# Revit family: Groeninger Window Drives
name_source: partatom
category: Fenster
units: mm (PartAtom-declared; Revit-internal decimal feet)

## family parameters
Basisbauteil = Fläche
Beim Laden mit Abzugskörper schneiden = Nein
Gemeinsam genutzt = Nein
OmniClass-Nummer = 23.30.20.11
OmniClass-Titel = Window Components
Raumberechnungspunkt = Nein

## types (1)
- Window actuator DK-100 (Art. No. G1001000)
    Accessories = No additional components required, such as brackets for drive attachment or elements for transmitting the drive force, are required
    Building Management System / Smart Home = Integration into the building management system through potential-free normally open contact (digital IO)
    Center sealing = Center sealing systems required
    City = Aichtal
    Control = Pushbuttons, switches, dead man's buttons
    Country = Germany
    Description = Window drive for automated tilt-opening and tilt-closing including locking and unlocking, with full retention of manual operation in any window position and completely concealed frame mounting
    Detection of window position = Detection of the window position integrated in the drive during automatic and manual operation
    Duty cycle (DIN EN 60034-1) = S3 25%; S2 2min
    End positions = Automated referencing of end positions
    Fastening = Sufficient material available for screw fastening
    Groove position = 13mm
    Hersteller = Groeninger Antriebstechnik GmbH & Co. KG
    Hinge side = Hinge side right and left possible
    Installation position = Completely concealed drive milled into the profile, invisible in closed position
    Lifetime = Tested with 20,000 switching cycles (double stroke incl. locking)
    Manual operation = Manual operation of all window positions (tilt position, turning position, closed position) by window handle possible from any position (window handle permanently mounted)
    Modell = Fensterantrieb DK-100 (Art. Nr.: G1001000)
    Opening / Closing Time = approx. 28s in normal mode and approx. 35s in slow mode
    Opening and closing force = 800N via the locking bar
    Opening width = Tilt opening width between 100 mm and 130 mm depending on the fitting used
    Possible fittings = Winkhaus activPilot Ergo, Maco Multi Comfort Fitting
    Rated current consumption = 0.75 A
    Rebate space = 12-14mm
    Reduced speed = Slow mode adjustable via DIP switch to realize quiet running noise
    Risidual ripple = max. 2Vp-p
    Scope of delivery = Drive
Connecting cable 3m PVC
Fastening screws for plastic windows
Cover connection area incl. strain relief and screws
Magnet for position detection
Sticker "Power-operated window"
    Space = Installation space Available in the lower frame piece
    Street = Alte Str. 9
    Supply voltage by external power supply = 24V DC
    Telephone = +49 7127 9606380
    URL = www.fenster-antrieb.de
    Vorgabe-Ansicht = 0 mm  [stored 0 ft]
    Website = www.fenster-antrieb.de
    Window type = Suitable for rectangular tilt-and-turn windows made of wood, plastic or aluminium
    Zip code = 72631
    max. sash weight = 60 kg

note: [stored X ft] marks values corroborated as IEEE doubles in the binary element streams (Revit-internal decimal feet)
